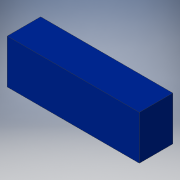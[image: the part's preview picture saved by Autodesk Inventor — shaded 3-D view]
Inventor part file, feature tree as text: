
AUTODESK INVENTOR PART (.ipt)
format: ipt  version: 2019.3 (Build 233278000, 278)  size: 101,888 bytes
history: native  units: mm
features: extrude x1, sketch x1
ambient origin geometry x8: Origin, YZ Plane, XZ Plane, XY Plane, X Axis, Y Axis, Z Axis, Center Point
bodies: Solid1 (feature_tree)
feature tree (2):
  extrude  "Extrusion1"  Depth=50.0mm
  sketch  "Sketch1"  dims[d0=150.0mm d1=50.0mm d2=38.0mm d3=0.0mm]
